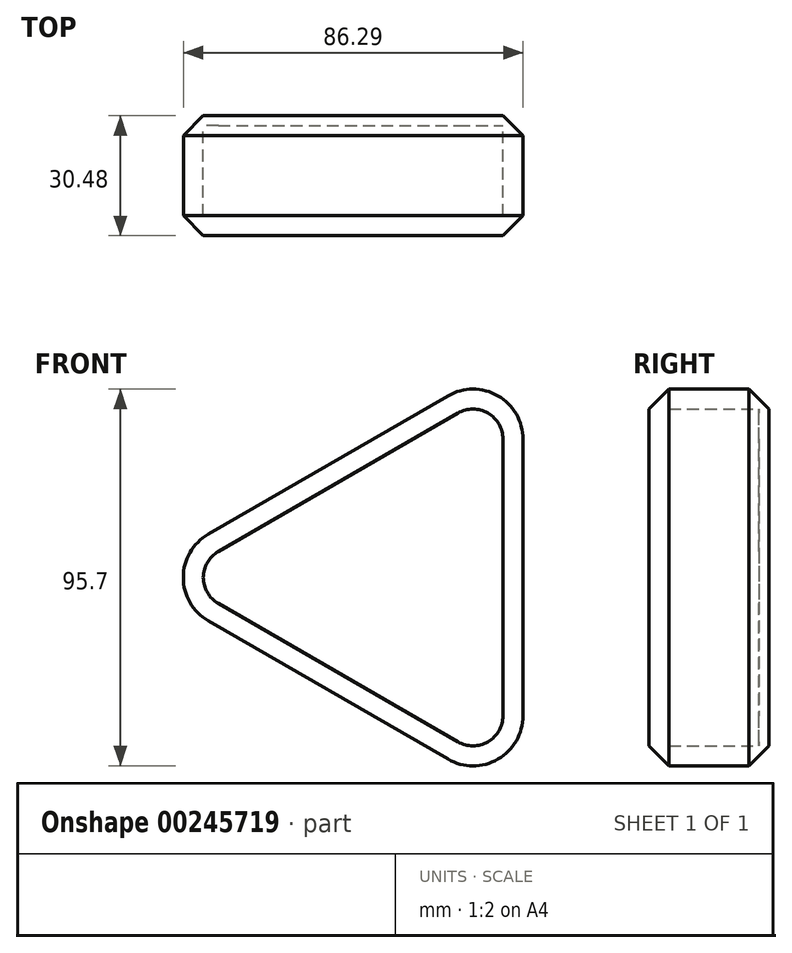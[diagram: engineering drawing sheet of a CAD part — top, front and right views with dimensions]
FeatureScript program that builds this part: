
annotation { "Feature Type Name" : "Feature", "Feature Type Description" : "" }
export const myFeature = defineFeature(function(context is Context, id is Id, definition is map)
    precondition{}
    {
        {
            var Q0;
            Q0=qCreatedBy(makeId("Front.planeOp"),FACE);
            var sketch = newSketch(context, id + "F0", { "sketchPlane" : qUnion([Q0])});
            skCircle(sketch, "E0.cCircle", {"center": v(0, 0) * mm, "radius": 33 * mm, "construction": true});
            skLineSegment(sketch, "E0.0", {"start": v(33, 57.15) * mm, "end": v(33, -57.15) * mm});
            skLineSegment(sketch, "E0.1", {"start": v(33, -57.15) * mm, "end": v(-66, 0) * mm});
            skLineSegment(sketch, "E0.2", {"start": v(-66, 0) * mm, "end": v(33, 57.15) * mm});
            skPoint(sketch, "E0.0.midPoint", {"position": v(33, 0) * mm});
            skSolve(sketch);
        }
        {
            var Q0;
            Q0=makeQuery(id+"F0.imprint","IMPRINT",FACE,{"disambiguationData":[TD([[makeQuery(id+"F0.imprint","IMPRINT",EDGE,{"derivedFrom":sQuery(id+"F0.wireOp",EDGE,"E0.0")}),-1.0]])]});
            extrude(context, id + "F8", {"entities" : qUnion([Q0]), "depth" : 25.4 * mm});
        }
        {
            var Q0;
            Q0=makeQuery(id+"F8.opExtrude","SWEPT_EDGE",EDGE,{"disambiguationData":[OSD([sQuery(id+"F0.wireOp",EDGE,"E0.0"),sQuery(id+"F0.wireOp",EDGE,"E0.2")])]});
            var Q1;
            Q1=makeQuery(id+"F8.opExtrude","SWEPT_EDGE",EDGE,{"disambiguationData":[OSD([sQuery(id+"F0.wireOp",EDGE,"E0.0"),sQuery(id+"F0.wireOp",EDGE,"E0.1")])]});
            var Q2;
            Q2=makeQuery(id+"F8.opExtrude","SWEPT_EDGE",EDGE,{"disambiguationData":[OSD([sQuery(id+"F0.wireOp",EDGE,"E0.1"),sQuery(id+"F0.wireOp",EDGE,"E0.2")])]});
            fillet(context, id + "F1", {"entities" : qUnion([Q0, Q1, Q2]), "radius" : 12.7 * mm, "tangentPropagation" : true, "allowEdgeOverflow" : false});
        }
        {
            var Q0;
            Q0=makeQuery(id+"F8.opExtrude","CAP_FACE",FACE,{"disambiguationData":[OSD([sQuery(id+"F0.wireOp",EDGE,"E0.0"),sQuery(id+"F0.wireOp",EDGE,"E0.1"),sQuery(id+"F0.wireOp",EDGE,"E0.2")])],"isStart":false});
            shell(context, id + "F9", {"entities" : qUnion([Q0]), "thickness" : 2.54 * mm});
        }
        {
            var Q0;
            Q0=makeQuery(id+"F9.opShell","OFFSET_FACE",FACE,{"disambiguationData":[OSD([sQuery(id+"F0.wireOp",EDGE,"E0.0"),sQuery(id+"F0.wireOp",EDGE,"E0.1"),sQuery(id+"F0.wireOp",EDGE,"E0.2")])]});
            var sketch = newSketch(context, id + "F2", { "sketchPlane" : qUnion([Q0])});
            skLineSegment(sketch, "E1.0", {"start": v(-45.67, 8.8) * mm, "end": v(15.22, 43.95) * mm});
            skArc(sketch, "E2.0", {"start": v(15.22, 43.95) * mm, "mid": v(25.38, 43.95) * mm, "end": v(30.46, 35.15) * mm});
            skLineSegment(sketch, "E3.0", {"start": v(30.46, 35.15) * mm, "end": v(30.46, -35.15) * mm});
            skArc(sketch, "E4.0", {"start": v(30.46, -35.15) * mm, "mid": v(25.38, -43.95) * mm, "end": v(15.22, -43.95) * mm});
            skLineSegment(sketch, "E5.0", {"start": v(15.22, -43.95) * mm, "end": v(-45.67, -8.8) * mm});
            skArc(sketch, "E6.0", {"start": v(-45.67, -8.8) * mm, "mid": v(-50.75, 0) * mm, "end": v(-45.67, 8.8) * mm});
            skArc(sketch, "E7.0", {"start": v(27.92, -35.15) * mm, "mid": v(24.1, -41.75) * mm, "end": v(16.49, -41.75) * mm});
            skArc(sketch, "E7.1", {"start": v(-44.4, -6.6) * mm, "mid": v(-48.21, 0) * mm, "end": v(-44.4, 6.6) * mm});
            skLineSegment(sketch, "E7.2", {"start": v(-44.4, 6.6) * mm, "end": v(16.49, 41.75) * mm});
            skLineSegment(sketch, "E7.3", {"start": v(16.49, -41.75) * mm, "end": v(-44.4, -6.6) * mm});
            skArc(sketch, "E7.4", {"start": v(16.49, 41.75) * mm, "mid": v(24.1, 41.75) * mm, "end": v(27.92, 35.15) * mm});
            skLineSegment(sketch, "E7.5", {"start": v(27.92, 35.15) * mm, "end": v(27.92, -35.15) * mm});
            skSolve(sketch);
        }
        {
            var Q0;
            Q0=makeQuery(id+"F2.imprint","IMPRINT",FACE,{"disambiguationData":[TD([[makeQuery(id+"F2.imprint","IMPRINT",EDGE,{"derivedFrom":sQuery(id+"F2.wireOp",EDGE,"E1.0")}),-1.0]])]});
            extrude(context, id + "F10", {"entities" : qUnion([Q0]), "operationType" : NewBodyOperationType.ADD, "depth" : 2.54 * mm});
        }
        {
            var Q0;
            Q0=makeQuery(id+"F10.opExtrude","CAP_FACE",FACE,{"disambiguationData":[OSD([sQuery(id+"F2.wireOp",EDGE,"E1.0"),sQuery(id+"F2.wireOp",EDGE,"E2.0"),sQuery(id+"F2.wireOp",EDGE,"E3.0"),sQuery(id+"F2.wireOp",EDGE,"E4.0"),sQuery(id+"F2.wireOp",EDGE,"E5.0"),sQuery(id+"F2.wireOp",EDGE,"E6.0"),sQuery(id+"F2.wireOp",EDGE,"E7.0"),sQuery(id+"F2.wireOp",EDGE,"E7.1"),sQuery(id+"F2.wireOp",EDGE,"E7.2"),sQuery(id+"F2.wireOp",EDGE,"E7.3"),sQuery(id+"F2.wireOp",EDGE,"E7.4"),sQuery(id+"F2.wireOp",EDGE,"E7.5")])],"isStart":false});
            extrude(context, id + "F3", {"entities" : qUnion([Q0]), "depth" : 20.32 * mm});
        }
        {
            var Q0;
            Q0=makeQuery(id+"F8.opExtrude","CAP_FACE",FACE,{"disambiguationData":[OSD([sQuery(id+"F0.wireOp",EDGE,"E0.0"),sQuery(id+"F0.wireOp",EDGE,"E0.1"),sQuery(id+"F0.wireOp",EDGE,"E0.2")])],"isStart":false});
            var sketch = newSketch(context, id + "F4", { "sketchPlane" : qUnion([Q0])});
            skLineSegment(sketch, "E8.0", {"start": v(33, 35.15) * mm, "end": v(33, -35.15) * mm});
            skArc(sketch, "E9.0", {"start": v(13.95, -46.15) * mm, "mid": v(26.65, -46.15) * mm, "end": v(33, -35.15) * mm});
            skLineSegment(sketch, "E10.0", {"start": v(13.95, -46.15) * mm, "end": v(-46.94, -11) * mm});
            skArc(sketch, "E11.0", {"start": v(-46.94, 11) * mm, "mid": v(-53.3, 0) * mm, "end": v(-46.94, -11) * mm});
            skLineSegment(sketch, "E12.0", {"start": v(-46.94, 11) * mm, "end": v(13.95, 46.15) * mm});
            skArc(sketch, "E13.0", {"start": v(33, 35.15) * mm, "mid": v(26.65, 46.15) * mm, "end": v(13.95, 46.15) * mm});
            skSolve(sketch);
        }
        {
            var Q0;
            Q0 = qSketchRegion(id + "F4", true);
            extrude(context, id + "F5", {"entities" : qUnion([Q0]), "operationType" : NewBodyOperationType.ADD, "depth" : 5.08 * mm});
        }
        {
            var Q0;
            Q0=makeQuery(id+"F5.opExtrude","CAP_EDGE",EDGE,{"disambiguationData":[OSD([sQuery(id+"F4.wireOp",EDGE,"E11.0")])],"isStart":false});
            chamfer(context, id + "F6", {"entities" : qUnion([Q0]), "width" : 5.08 * mm, "tangentPropagation" : true});
        }
        {
            var Q0;
            Q0=makeQuery(id+"F8.opExtrude","CAP_EDGE",EDGE,{"disambiguationData":[OSD([sQuery(id+"F0.wireOp",EDGE,"E0.1")])],"isStart":true});
            chamfer(context, id + "F7", {"entities" : qUnion([Q0]), "width" : 5.08 * mm, "tangentPropagation" : true});
        }
    });
